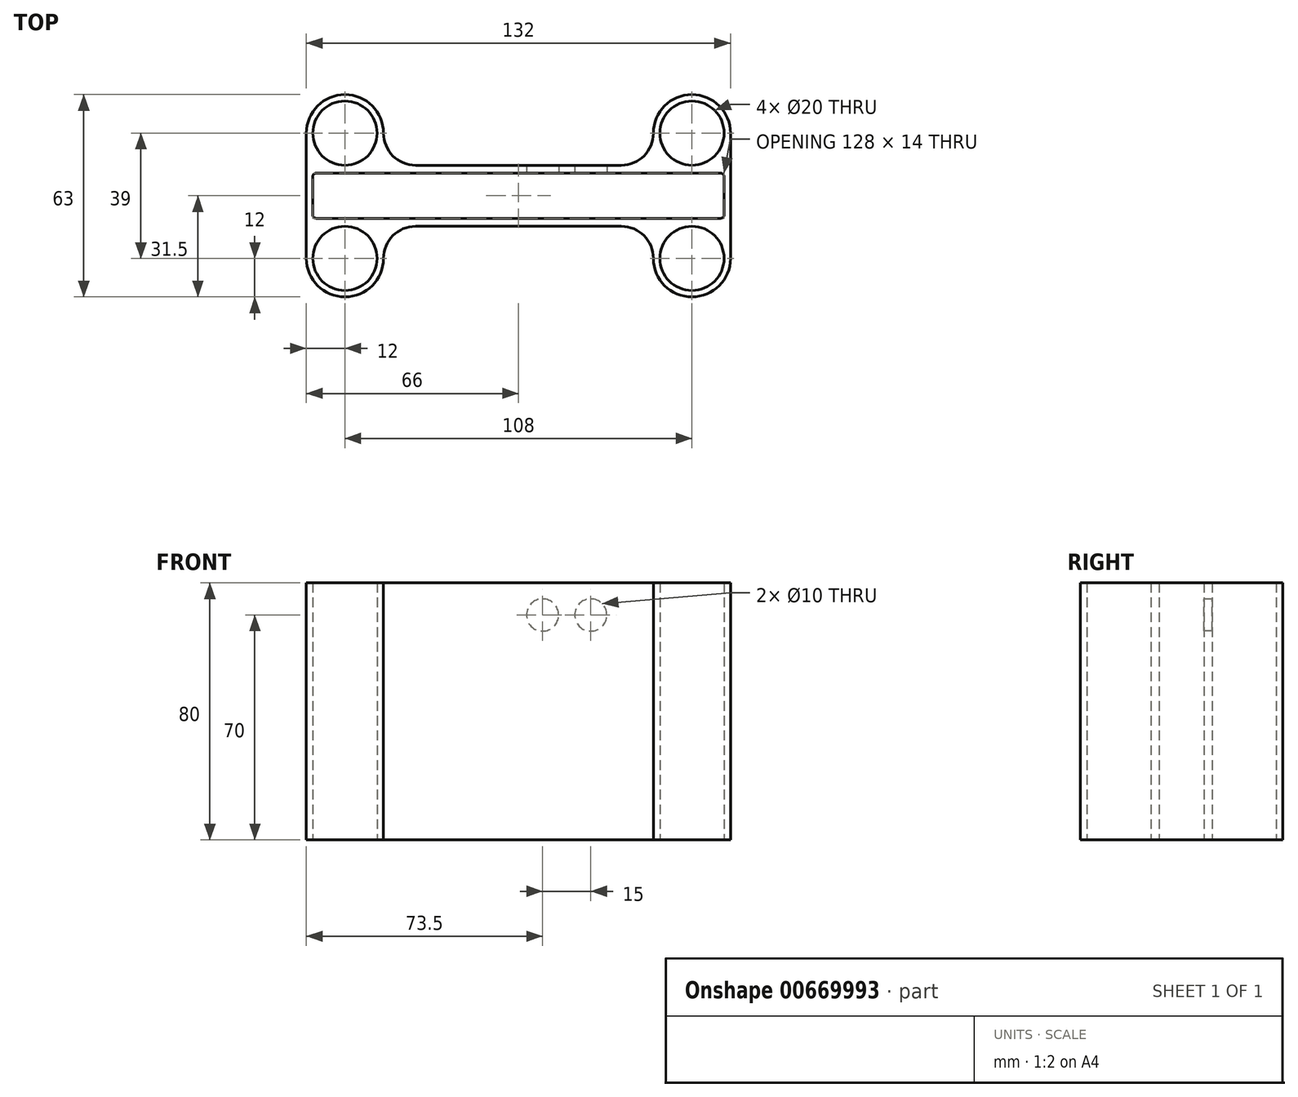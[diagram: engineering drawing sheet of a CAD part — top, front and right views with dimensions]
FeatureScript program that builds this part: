
annotation { "Feature Type Name" : "Feature", "Feature Type Description" : "" }
export const myFeature = defineFeature(function(context is Context, id is Id, definition is map)
    precondition{}
    {
        {
            var Q0;
            Q0=qCreatedBy(makeId("Top.planeOp"),FACE);
            var sketch = newSketch(context, id + "F0", { "sketchPlane" : qUnion([Q0])});
            skLineSegment(sketch, "E0.bottom", {"start": v(62, 5) * mm, "end": v(-62, 5) * mm, "construction": true});
            skLineSegment(sketch, "E0.top", {"start": v(62, -5) * mm, "end": v(-62, -5) * mm, "construction": true});
            skLineSegment(sketch, "E0.left", {"start": v(62, 5) * mm, "end": v(62, -5) * mm, "construction": true});
            skLineSegment(sketch, "E0.right", {"start": v(-62, 5) * mm, "end": v(-62, -5) * mm, "construction": true});
            skPoint(sketch, "E0.middle", {"position": v(0, 0) * mm});
            skLineSegment(sketch, "E1.0", {"start": v(63, 7) * mm, "end": v(-63, 7) * mm});
            skLineSegment(sketch, "E1.1", {"start": v(64, 6) * mm, "end": v(64, -6) * mm});
            skLineSegment(sketch, "E1.2", {"start": v(63, -7) * mm, "end": v(-63, -7) * mm});
            skLineSegment(sketch, "E1.3", {"start": v(-64, 6) * mm, "end": v(-64, -6) * mm});
            skLineSegment(sketch, "E2.1", {"start": v(66, 19.5) * mm, "end": v(66, -19.5) * mm});
            skLineSegment(sketch, "E2.2", {"start": v(32, -9.5) * mm, "end": v(-32, -9.5) * mm});
            skLineSegment(sketch, "E2.3", {"start": v(-66, 19.5) * mm, "end": v(-66, -19.5) * mm});
            skCircle(sketch, "E3", {"center": v(-54, -19.5) * mm, "radius": 10 * mm});
            skArc(sketch, "E4", {"start": v(-42, -19.5) * mm, "mid": v(-54, -31.5) * mm, "end": v(-66, -19.5) * mm});
            skLineSegment(sketch, "E5", {"start": v(-42, -19.5) * mm, "end": v(-42, -19.5) * mm});
            skArc(sketch, "E6.filletArc", {"start": v(-32, -9.5) * mm, "mid": v(-39.07, -12.43) * mm, "end": v(-42, -19.5) * mm});
            skArc(sketch, "E7.MirrorCS", {"start": v(-32, 9.5) * mm, "mid": v(-39.07, 12.43) * mm, "end": v(-42, 19.5) * mm});
            skArc(sketch, "E8.MirrorCS", {"start": v(-42, 19.5) * mm, "mid": v(-54, 31.5) * mm, "end": v(-66, 19.5) * mm});
            skCircle(sketch, "E9.MirrorC", {"center": v(-54, 19.5) * mm, "radius": 10 * mm});
            skCircle(sketch, "E10.MirrorC", {"center": v(54, -19.5) * mm, "radius": 10 * mm});
            skCircle(sketch, "E11.MirrorC", {"center": v(54, 19.5) * mm, "radius": 10 * mm});
            skArc(sketch, "E12.MirrorCS", {"start": v(32, 9.5) * mm, "mid": v(39.07, 12.43) * mm, "end": v(42, 19.5) * mm});
            skArc(sketch, "E13.MirrorCS", {"start": v(42, 19.5) * mm, "mid": v(54, 31.5) * mm, "end": v(66, 19.5) * mm});
            skArc(sketch, "E14.MirrorCS", {"start": v(42, -19.5) * mm, "mid": v(54, -31.5) * mm, "end": v(66, -19.5) * mm});
            skArc(sketch, "E15.MirrorCS", {"start": v(32, -9.5) * mm, "mid": v(39.07, -12.43) * mm, "end": v(42, -19.5) * mm});
            skLineSegment(sketch, "E16.trimOffspring", {"start": v(32, 9.5) * mm, "end": v(-32, 9.5) * mm});
            skPoint(sketch, "E17.visualSharp", {"position": v(-64, 7) * mm});
            skArc(sketch, "E17.filletArc", {"start": v(-63, 7) * mm, "mid": v(-63.7, 6.7) * mm, "end": v(-64, 6) * mm});
            skPoint(sketch, "E18.visualSharp", {"position": v(-64, -7) * mm});
            skArc(sketch, "E18.filletArc", {"start": v(-64, -6) * mm, "mid": v(-63.7, -6.7) * mm, "end": v(-63, -7) * mm});
            skPoint(sketch, "E19.visualSharp", {"position": v(64, -7) * mm});
            skArc(sketch, "E19.filletArc", {"start": v(63, -7) * mm, "mid": v(63.7, -6.7) * mm, "end": v(64, -6) * mm});
            skPoint(sketch, "E20.visualSharp", {"position": v(64, 7) * mm});
            skArc(sketch, "E20.filletArc", {"start": v(64, 6) * mm, "mid": v(63.7, 6.7) * mm, "end": v(63, 7) * mm});
            skLineSegment(sketch, "E21", {"start": v(42, 19.5) * mm, "end": v(42, 7) * mm});
            skLineSegment(sketch, "E22", {"start": v(-64, 19.5) * mm, "end": v(-64, 7) * mm});
            skLineSegment(sketch, "E23", {"start": v(-66, 7) * mm, "end": v(-64, 7) * mm});
            skLineSegment(sketch, "E24", {"start": v(-42, 19.5) * mm, "end": v(-42, 7) * mm});
            skLineSegment(sketch, "E25", {"start": v(-44, 19.5) * mm, "end": v(-44, 7) * mm});
            skLineSegment(sketch, "E26", {"start": v(-64, -19.5) * mm, "end": v(-64, -7) * mm});
            skLineSegment(sketch, "E27", {"start": v(-64, -7) * mm, "end": v(-66, -6.9) * mm});
            skLineSegment(sketch, "E28", {"start": v(-44, -19.5) * mm, "end": v(-44, -7) * mm});
            skLineSegment(sketch, "E29", {"start": v(-42, -19.5) * mm, "end": v(-42, -7) * mm});
            skLineSegment(sketch, "E30", {"start": v(44, -19.5) * mm, "end": v(44, -7) * mm});
            skLineSegment(sketch, "E31", {"start": v(42, -19.5) * mm, "end": v(42, -7) * mm});
            skLineSegment(sketch, "E32", {"start": v(64, -19.5) * mm, "end": v(64, -7) * mm});
            skLineSegment(sketch, "E33", {"start": v(64, -7) * mm, "end": v(66, -7) * mm});
            skLineSegment(sketch, "E34", {"start": v(44, 19.5) * mm, "end": v(44, 7) * mm});
            skLineSegment(sketch, "E35", {"start": v(64, 19.5) * mm, "end": v(64, 7) * mm});
            skLineSegment(sketch, "E36", {"start": v(64, 7) * mm, "end": v(66, 7) * mm});
            skSolve(sketch);
        }
        {
            var Q0;
            Q0 = qSketchRegion(id + "F0", true);
            extrude(context, id + "F1", {"entities" : qUnion([Q0]), "depth" : 80 * mm, "offsetDistance" : 25 * mm});
        }
        {
            var Q0;
            Q0=qCreatedBy(makeId("Front.planeOp"),FACE);
            var sketch = newSketch(context, id + "F2", { "sketchPlane" : qUnion([Q0])});
            skLineSegment(sketch, "E37.0.1", {"start": v(66, 0) * mm, "end": v(66, 80) * mm});
            skLineSegment(sketch, "E37.0.3", {"start": v(66, 80) * mm, "end": v(66, 0) * mm});
            skLineSegment(sketch, "E38.0.1", {"start": v(-66, 0) * mm, "end": v(-66, 80) * mm});
            skLineSegment(sketch, "E38.0.3", {"start": v(-66, 80) * mm, "end": v(-66, 0) * mm});
            skLineSegment(sketch, "E39.0.0", {"start": v(32, 0) * mm, "end": v(-32, 0) * mm});
            skLineSegment(sketch, "E39.0.1", {"start": v(-32, 0) * mm, "end": v(-32, 80) * mm});
            skLineSegment(sketch, "E39.0.2", {"start": v(-32, 80) * mm, "end": v(32, 80) * mm});
            skLineSegment(sketch, "E39.0.3", {"start": v(32, 80) * mm, "end": v(32, 0) * mm});
            skLineSegment(sketch, "E40.0.0", {"start": v(-66, 0) * mm, "end": v(-42, 0) * mm});
            skLineSegment(sketch, "E40.0.2", {"start": v(-42, 80) * mm, "end": v(-66, 80) * mm});
            skLineSegment(sketch, "E40.0.3", {"start": v(-42, 80) * mm, "end": v(-42, 0) * mm});
            skLineSegment(sketch, "E41.0.0", {"start": v(42, 0) * mm, "end": v(66, 0) * mm});
            skLineSegment(sketch, "E41.0.1", {"start": v(42, 0) * mm, "end": v(42, 80) * mm});
            skLineSegment(sketch, "E41.0.2", {"start": v(66, 80) * mm, "end": v(42, 80) * mm});
            skLineSegment(sketch, "E42", {"start": v(54, 80) * mm, "end": v(54, 0) * mm, "construction": true});
            skLineSegment(sketch, "E43", {"start": v(-54, 80) * mm, "end": v(-54, 0) * mm, "construction": true});
            skCircle(sketch, "E44", {"center": v(54, 70) * mm, "radius": 5 * mm});
            skCircle(sketch, "E45", {"center": v(-54, 70) * mm, "radius": 5 * mm});
            skCircle(sketch, "E46", {"center": v(22.5, 70) * mm, "radius": 5 * mm});
            skCircle(sketch, "E47", {"center": v(7.5, 70) * mm, "radius": 5 * mm});
            skCircle(sketch, "E48", {"center": v(-7.5, 70) * mm, "radius": 5 * mm});
            skCircle(sketch, "E49", {"center": v(-22.5, 70) * mm, "radius": 5 * mm});
            skCircle(sketch, "E50.0.1.0", {"center": v(54, 55) * mm, "radius": 5 * mm});
            skCircle(sketch, "E50.0.1.1", {"center": v(22.5, 55) * mm, "radius": 5 * mm});
            skCircle(sketch, "E50.0.1.2", {"center": v(7.5, 55) * mm, "radius": 5 * mm});
            skCircle(sketch, "E50.0.1.3", {"center": v(-7.5, 55) * mm, "radius": 5 * mm});
            skCircle(sketch, "E50.0.1.4", {"center": v(-22.5, 55) * mm, "radius": 5 * mm});
            skCircle(sketch, "E50.0.1.5", {"center": v(-54, 55) * mm, "radius": 5 * mm});
            skCircle(sketch, "E50.0.2.0", {"center": v(54, 40) * mm, "radius": 5 * mm});
            skCircle(sketch, "E50.0.2.1", {"center": v(22.5, 40) * mm, "radius": 5 * mm});
            skCircle(sketch, "E50.0.2.2", {"center": v(7.5, 40) * mm, "radius": 5 * mm});
            skCircle(sketch, "E50.0.2.3", {"center": v(-7.5, 40) * mm, "radius": 5 * mm});
            skCircle(sketch, "E50.0.2.4", {"center": v(-22.5, 40) * mm, "radius": 5 * mm});
            skCircle(sketch, "E50.0.2.5", {"center": v(-54, 40) * mm, "radius": 5 * mm});
            skCircle(sketch, "E50.0.3.0", {"center": v(54, 25) * mm, "radius": 5 * mm});
            skCircle(sketch, "E50.0.3.1", {"center": v(22.5, 25) * mm, "radius": 5 * mm});
            skCircle(sketch, "E50.0.3.2", {"center": v(7.5, 25) * mm, "radius": 5 * mm});
            skCircle(sketch, "E50.0.3.3", {"center": v(-7.5, 25) * mm, "radius": 5 * mm});
            skCircle(sketch, "E50.0.3.4", {"center": v(-22.5, 25) * mm, "radius": 5 * mm});
            skCircle(sketch, "E50.0.3.5", {"center": v(-54, 25) * mm, "radius": 5 * mm});
            skCircle(sketch, "E50.0.4.0", {"center": v(54, 10) * mm, "radius": 5 * mm});
            skCircle(sketch, "E50.0.4.1", {"center": v(22.5, 10) * mm, "radius": 5 * mm});
            skCircle(sketch, "E50.0.4.2", {"center": v(7.5, 10) * mm, "radius": 5 * mm});
            skCircle(sketch, "E50.0.4.3", {"center": v(-7.5, 10) * mm, "radius": 5 * mm});
            skCircle(sketch, "E50.0.4.4", {"center": v(-22.5, 10) * mm, "radius": 5 * mm});
            skCircle(sketch, "E50.0.4.5", {"center": v(-54, 10) * mm, "radius": 5 * mm});
            skLineSegment(sketch, "E50.direction1", {"start": v(54, 70) * mm, "end": v(79, 70) * mm, "construction": true});
            skLineSegment(sketch, "E50.direction2", {"start": v(54, 70) * mm, "end": v(54, 55) * mm, "construction": true});
            skSolve(sketch);
        }
        {
            var Q0;
            Q0=makeQuery(id+"F2.imprint","IMPRINT",FACE,{"disambiguationData":[TD([[makeQuery(id+"F2.imprint","IMPRINT",EDGE,{"derivedFrom":sQuery(id+"F2.wireOp",EDGE,"E46")}),1.0]])]});
            var Q1;
            Q1=makeQuery(id+"F2.imprint","IMPRINT",FACE,{"disambiguationData":[TD([[makeQuery(id+"F2.imprint","IMPRINT",EDGE,{"derivedFrom":sQuery(id+"F2.wireOp",EDGE,"E47")}),1.0]])]});
            extrude(context, id + "F3", {"entities" : qUnion([Q0, Q1]), "operationType" : NewBodyOperationType.REMOVE, "oppositeDirection" : true, "depth" : 25 * mm, "offsetDistance" : 25 * mm});
        }
    });
